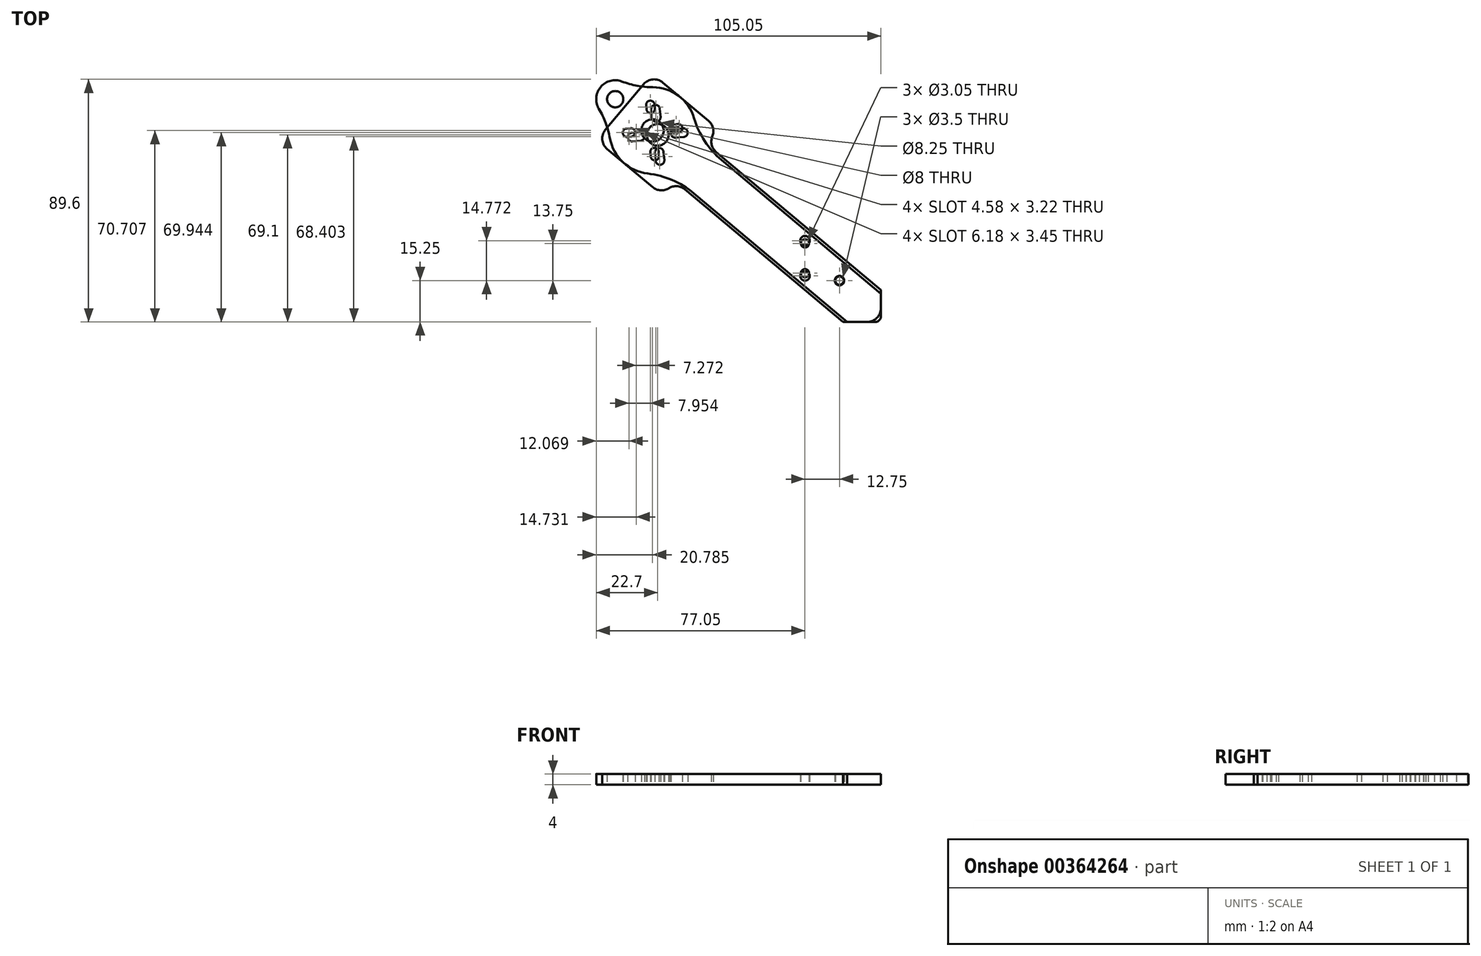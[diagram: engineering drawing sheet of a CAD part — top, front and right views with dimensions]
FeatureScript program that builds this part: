
annotation { "Feature Type Name" : "Feature", "Feature Type Description" : "" }
export const myFeature = defineFeature(function(context is Context, id is Id, definition is map)
    precondition{}
    {
        {
            var Q0;
            Q0=qCreatedBy(makeId("Top.planeOp"),FACE);
            var sketch = newSketch(context, id + "F0", { "sketchPlane" : qUnion([Q0])});
            skCircle(sketch, "E0", {"center": v(0, 0) * mm, "radius": 107.5 * mm, "construction": true});
            skCircle(sketch, "E1", {"center": v(-82.35, 69.1) * mm, "radius": 63.5 * mm, "construction": true});
            skLineSegment(sketch, "E2", {"start": v(0, 0) * mm, "end": v(-82.35, 69.1) * mm, "construction": true});
            skCircle(sketch, "E3", {"center": v(-82.35, 69.1) * mm, "radius": 4 * mm});
            skLineSegment(sketch, "E4", {"start": v(-60.8, 62.76) * mm, "end": v(0, 11.75) * mm});
            skLineSegment(sketch, "E5", {"start": v(-72.37, 48.98) * mm, "end": v(-14, 0) * mm});
            skLineSegment(sketch, "E6.bottom", {"start": v(-101.68, 70.96) * mm, "end": v(-87.54, 87.81) * mm});
            skLineSegment(sketch, "E6.left", {"start": v(-101.06, 63.91) * mm, "end": v(-84.17, 49.74) * mm});
            skLineSegment(sketch, "E6.right", {"start": v(-80.5, 88.43) * mm, "end": v(-63.6, 74.26) * mm});
            skArc(sketch, "E7", {"start": v(-62.2, 68.51) * mm, "mid": v(-62.44, 65.4) * mm, "end": v(-60.8, 62.76) * mm});
            skArc(sketch, "E8", {"start": v(-72.37, 48.98) * mm, "mid": v(-75.26, 50.13) * mm, "end": v(-78.27, 49.36) * mm});
            skPoint(sketch, "E9.visualSharp", {"position": v(-104.9, 67.13) * mm});
            skArc(sketch, "E9.filletArc", {"start": v(-101.68, 70.96) * mm, "mid": v(-102.83, 67.3) * mm, "end": v(-101.06, 63.91) * mm});
            skPoint(sketch, "E10.visualSharp", {"position": v(-84.32, 91.64) * mm});
            skArc(sketch, "E10.filletArc", {"start": v(-80.5, 88.43) * mm, "mid": v(-84.14, 89.58) * mm, "end": v(-87.54, 87.81) * mm});
            skPoint(sketch, "E11.visualSharp", {"position": v(-80.38, 46.56) * mm});
            skArc(sketch, "E11.filletArc", {"start": v(-84.17, 49.74) * mm, "mid": v(-81.29, 48.59) * mm, "end": v(-78.27, 49.36) * mm});
            skPoint(sketch, "E12.visualSharp", {"position": v(-59.8, 71.07) * mm});
            skArc(sketch, "E12.filletArc", {"start": v(-62.2, 68.51) * mm, "mid": v(-61.96, 71.61) * mm, "end": v(-63.6, 74.26) * mm});
            skLineSegment(sketch, "E13", {"start": v(-83.18, 78.56) * mm, "end": v(-82.92, 75.57) * mm, "construction": true});
            skLineSegment(sketch, "E14", {"start": v(-82.35, 69.1) * mm, "end": v(-82.92, 75.57) * mm, "construction": true});
            skArc(sketch, "E15.0.startCap", {"start": v(-84.77, 78.42) * mm, "mid": v(-83.32, 80.16) * mm, "end": v(-81.58, 78.7) * mm});
            skArc(sketch, "E15.0.endCap", {"start": v(-81.32, 75.71) * mm, "mid": v(-82.78, 73.98) * mm, "end": v(-84.51, 75.44) * mm});
            skLineSegment(sketch, "E15.0.left", {"start": v(-81.58, 78.7) * mm, "end": v(-81.32, 75.71) * mm});
            skLineSegment(sketch, "E15.0.right", {"start": v(-84.77, 78.42) * mm, "end": v(-84.51, 75.44) * mm});
            skLineSegment(sketch, "E16.1.0", {"start": v(-91.95, 69.87) * mm, "end": v(-88.96, 70.13) * mm});
            skLineSegment(sketch, "E16.1.1", {"start": v(-91.81, 68.27) * mm, "end": v(-88.83, 68.53) * mm, "construction": true});
            skArc(sketch, "E16.1.2", {"start": v(-88.96, 70.13) * mm, "mid": v(-87.23, 68.67) * mm, "end": v(-88.69, 66.94) * mm});
            skArc(sketch, "E16.1.3", {"start": v(-91.67, 66.68) * mm, "mid": v(-93.4, 68.13) * mm, "end": v(-91.95, 69.87) * mm});
            skLineSegment(sketch, "E16.1.4", {"start": v(-91.67, 66.68) * mm, "end": v(-88.69, 66.94) * mm});
            skLineSegment(sketch, "E16.2.0", {"start": v(-83.12, 59.5) * mm, "end": v(-83.38, 62.48) * mm});
            skLineSegment(sketch, "E16.2.1", {"start": v(-81.52, 59.64) * mm, "end": v(-81.78, 62.62) * mm, "construction": true});
            skArc(sketch, "E16.2.2", {"start": v(-83.38, 62.48) * mm, "mid": v(-81.92, 64.22) * mm, "end": v(-80.19, 62.76) * mm});
            skArc(sketch, "E16.2.3", {"start": v(-79.93, 59.78) * mm, "mid": v(-81.38, 58.04) * mm, "end": v(-83.12, 59.5) * mm});
            skLineSegment(sketch, "E16.2.4", {"start": v(-79.93, 59.78) * mm, "end": v(-80.19, 62.76) * mm});
            skLineSegment(sketch, "E16.3.0", {"start": v(-72.75, 68.33) * mm, "end": v(-75.74, 68.07) * mm});
            skLineSegment(sketch, "E16.3.1", {"start": v(-72.89, 69.93) * mm, "end": v(-75.87, 69.67) * mm, "construction": true});
            skArc(sketch, "E16.3.2", {"start": v(-75.74, 68.07) * mm, "mid": v(-77.47, 69.53) * mm, "end": v(-76.01, 71.26) * mm});
            skArc(sketch, "E16.3.3", {"start": v(-73.03, 71.52) * mm, "mid": v(-71.3, 70.07) * mm, "end": v(-72.75, 68.33) * mm});
            skLineSegment(sketch, "E16.3.4", {"start": v(-73.03, 71.52) * mm, "end": v(-76.01, 71.26) * mm});
            skLineSegment(sketch, "E17", {"start": v(-14, 0) * mm, "end": v(0, 0) * mm});
            skLineSegment(sketch, "E18", {"start": v(0, 11.75) * mm, "end": v(0, 0) * mm});
            skCircle(sketch, "E19", {"center": v(-15.25, 15.25) * mm, "radius": 1.75 * mm});
            skCircle(sketch, "E20", {"center": v(-28, 16.97) * mm, "radius": 1.75 * mm});
            skCircle(sketch, "E21", {"center": v(-28, 30.02) * mm, "radius": 1.75 * mm});
            skSolve(sketch);
        }
        {
            var Q0;
            Q0=makeQuery(id+"F0.imprint","IMPRINT",FACE,{"disambiguationData":[TD([[makeQuery(id+"F0.imprint","IMPRINT",EDGE,{"derivedFrom":sQuery(id+"F0.wireOp",EDGE,"E3")}),-1.0]])]});
            extrude(context, id + "F1", {"entities" : qUnion([Q0]), "depth" : 4 * mm});
        }
        {
            var Q0;
            Q0=makeQuery(id+"F1.opExtrude","SWEPT_EDGE",EDGE,{"disambiguationData":[OSD([sQuery(id+"F0.wireOp",EDGE,"E17"),sQuery(id+"F0.wireOp",EDGE,"E18")])]});
            fillet(context, id + "F2", {"entities" : qUnion([Q0]), "radius" : 5 * mm, "tangentPropagation" : true, "allowEdgeOverflow" : false});
        }
        {
            var Q0;
            Q0=qCreatedBy(makeId("Top.planeOp"),FACE);
            var sketch = newSketch(context, id + "F3", { "sketchPlane" : qUnion([Q0])});
            skLineSegment(sketch, "E22", {"start": v(0, 0) * mm, "end": v(-84.26, 70.7) * mm, "construction": true});
            skArc(sketch, "E23", {"start": v(-68.92, 75.24) * mm, "mid": v(-74.67, 83.5) * mm, "end": v(-84.22, 86.7) * mm});
            skCircle(sketch, "E24", {"center": v(-84.26, 70.7) * mm, "radius": 4.12 * mm});
            skCircle(sketch, "E25", {"center": v(-84.26, 70.7) * mm, "radius": 8 * mm, "construction": true});
            skCircle(sketch, "E26", {"center": v(-84.26, 70.7) * mm, "radius": 9.5 * mm, "construction": true});
            skLineSegment(sketch, "E27", {"start": v(-84.26, 70.7) * mm, "end": v(-76.3, 71.4) * mm, "construction": true});
            skLineSegment(sketch, "E28", {"start": v(-76.3, 71.4) * mm, "end": v(-74.8, 71.53) * mm, "construction": true});
            skArc(sketch, "E29.0.startCap", {"start": v(-76.16, 69.86) * mm, "mid": v(-77.84, 71.27) * mm, "end": v(-76.43, 72.95) * mm});
            skArc(sketch, "E29.0.endCap", {"start": v(-74.94, 73.08) * mm, "mid": v(-73.26, 71.67) * mm, "end": v(-74.67, 70) * mm});
            skLineSegment(sketch, "E29.0.left", {"start": v(-76.43, 72.95) * mm, "end": v(-74.94, 73.08) * mm});
            skLineSegment(sketch, "E29.0.right", {"start": v(-76.16, 69.86) * mm, "end": v(-74.67, 70) * mm});
            skLineSegment(sketch, "E30.1.0", {"start": v(-86.5, 78.54) * mm, "end": v(-86.64, 80.04) * mm});
            skArc(sketch, "E30.1.1", {"start": v(-86.64, 80.04) * mm, "mid": v(-85.23, 81.71) * mm, "end": v(-83.55, 80.3) * mm});
            skLineSegment(sketch, "E30.1.2", {"start": v(-83.42, 78.81) * mm, "end": v(-83.55, 80.3) * mm});
            skArc(sketch, "E30.1.3", {"start": v(-83.42, 78.81) * mm, "mid": v(-84.83, 77.13) * mm, "end": v(-86.5, 78.54) * mm});
            skLineSegment(sketch, "E30.2.0", {"start": v(-92.1, 68.47) * mm, "end": v(-93.6, 68.33) * mm});
            skArc(sketch, "E30.2.1", {"start": v(-93.6, 68.33) * mm, "mid": v(-95.27, 69.74) * mm, "end": v(-93.86, 71.42) * mm});
            skLineSegment(sketch, "E30.2.2", {"start": v(-92.37, 71.55) * mm, "end": v(-93.86, 71.42) * mm});
            skArc(sketch, "E30.2.3", {"start": v(-92.37, 71.55) * mm, "mid": v(-90.7, 70.14) * mm, "end": v(-92.1, 68.47) * mm});
            skLineSegment(sketch, "E30.3.0", {"start": v(-82.02, 62.87) * mm, "end": v(-81.9, 61.38) * mm});
            skArc(sketch, "E30.3.1", {"start": v(-81.9, 61.38) * mm, "mid": v(-83.3, 59.7) * mm, "end": v(-84.98, 61.1) * mm});
            skLineSegment(sketch, "E30.3.2", {"start": v(-85.11, 62.6) * mm, "end": v(-84.98, 61.1) * mm});
            skArc(sketch, "E30.3.3", {"start": v(-85.11, 62.6) * mm, "mid": v(-83.7, 64.28) * mm, "end": v(-82.02, 62.87) * mm});
            skLineSegment(sketch, "E31", {"start": v(-58.8, 59.78) * mm, "end": v(0, 10.44) * mm});
            skLineSegment(sketch, "E32", {"start": v(-69.08, 47.52) * mm, "end": v(-12.45, 0) * mm});
            skLineSegment(sketch, "E33", {"start": v(-12.45, 0) * mm, "end": v(-2, 0) * mm});
            skLineSegment(sketch, "E34", {"start": v(0, 10.44) * mm, "end": v(0, 2) * mm});
            skPoint(sketch, "E35.visualSharp", {"position": v(-78.8, 55.67) * mm});
            skArc(sketch, "E35.filletArc", {"start": v(-69.08, 47.52) * mm, "mid": v(-77.03, 52.42) * mm, "end": v(-86.06, 54.8) * mm});
            skPoint(sketch, "E36.visualSharp", {"position": v(-68.5, 67.93) * mm});
            skArc(sketch, "E36.filletArc", {"start": v(-68.92, 75.24) * mm, "mid": v(-65, 66.76) * mm, "end": v(-58.8, 59.78) * mm});
            skCircle(sketch, "E37", {"center": v(-98.05, 82.28) * mm, "radius": 3 * mm});
            skLineSegment(sketch, "E38", {"start": v(-98.05, 82.28) * mm, "end": v(-84.26, 70.7) * mm, "construction": true});
            skArc(sketch, "E39", {"start": v(-95.55, 88.82) * mm, "mid": v(-103.42, 86.78) * mm, "end": v(-104.06, 78.68) * mm});
            skArc(sketch, "E40.trimOffspring", {"start": v(-100.01, 67.88) * mm, "mid": v(-95.2, 59.03) * mm, "end": v(-86.06, 54.8) * mm});
            skPoint(sketch, "E41.visualSharp", {"position": v(-99.55, 75.44) * mm});
            skArc(sketch, "E41.filletArc", {"start": v(-100.01, 67.88) * mm, "mid": v(-101.55, 73.47) * mm, "end": v(-104.06, 78.68) * mm});
            skPoint(sketch, "E42.visualSharp", {"position": v(-91.58, 84.94) * mm});
            skArc(sketch, "E42.filletArc", {"start": v(-95.55, 88.82) * mm, "mid": v(-89.98, 87.25) * mm, "end": v(-84.22, 86.7) * mm});
            skCircle(sketch, "E43", {"center": v(-15.25, 15.25) * mm, "radius": 1.52 * mm});
            skCircle(sketch, "E44", {"center": v(-28, 29) * mm, "radius": 1.52 * mm});
            skCircle(sketch, "E45", {"center": v(-28, 18) * mm, "radius": 1.52 * mm});
            skPoint(sketch, "E46.visualSharp", {"position": v(0, 0) * mm});
            skArc(sketch, "E46.filletArc", {"start": v(-2, 0) * mm, "mid": v(-0.59, 0.59) * mm, "end": v(0, 2) * mm});
            skCircle(sketch, "E47", {"center": v(-28, 29) * mm, "radius": 3 * mm, "construction": true});
            skCircle(sketch, "E48", {"center": v(-28, 18) * mm, "radius": 3 * mm, "construction": true});
            skSolve(sketch);
        }
        {
            var Q0;
            Q0=makeQuery(id+"F3.imprint","IMPRINT",FACE,{"disambiguationData":[TD([[makeQuery(id+"F3.imprint","IMPRINT",EDGE,{"derivedFrom":sQuery(id+"F3.wireOp",EDGE,"E23")}),1.0]])]});
            extrude(context, id + "F4", {"entities" : qUnion([Q0]), "depth" : 4 * mm, "offsetDistance" : 25 * mm});
        }
    });
